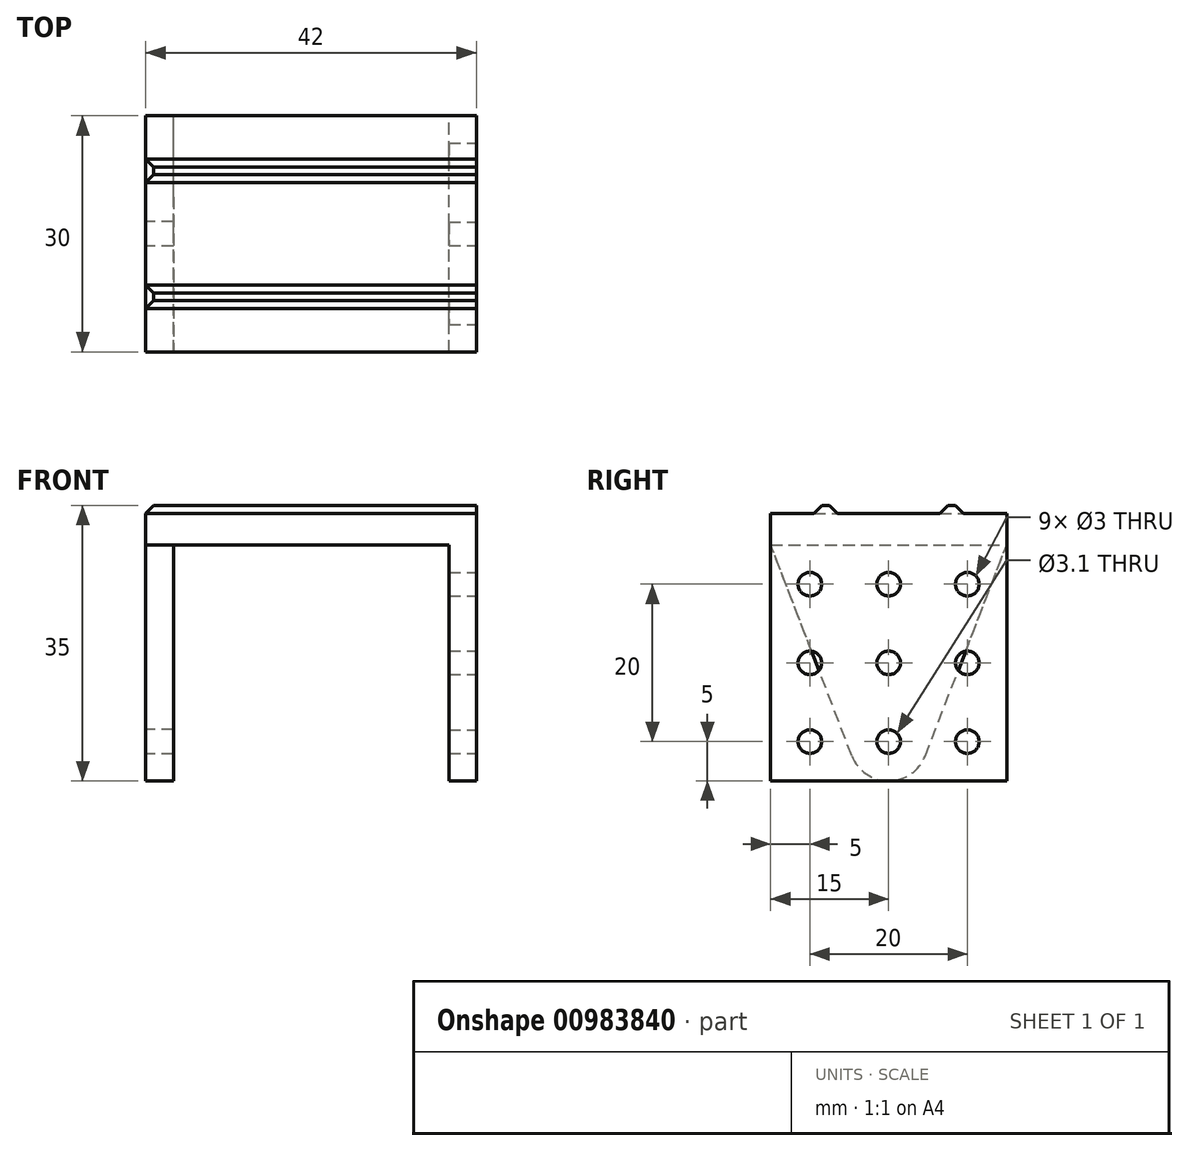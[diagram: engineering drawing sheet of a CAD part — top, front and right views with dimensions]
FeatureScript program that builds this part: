
annotation { "Feature Type Name" : "Feature", "Feature Type Description" : "" }
export const myFeature = defineFeature(function(context is Context, id is Id, definition is map)
    precondition{}
    {
        {
            var Q0;
            Q0=qCreatedBy(makeId("Top.planeOp"),FACE);
            var sketch = newSketch(context, id + "F0", { "sketchPlane" : qUnion([Q0])});
            skLineSegment(sketch, "E0.bottom", {"start": v(21, -15) * mm, "end": v(-21, -15) * mm});
            skLineSegment(sketch, "E0.top", {"start": v(21, 15) * mm, "end": v(-21, 15) * mm});
            skLineSegment(sketch, "E0.left", {"start": v(21, -15) * mm, "end": v(21, 15) * mm});
            skLineSegment(sketch, "E0.right", {"start": v(-21, -15) * mm, "end": v(-21, 15) * mm});
            skPoint(sketch, "E0.middle", {"position": v(0, 0) * mm});
            skSolve(sketch);
        }
        {
            var Q0;
            Q0 = qSketchRegion(id + "F0", true);
            extrude(context, id + "F1", {"entities" : qUnion([Q0]), "depth" : 4 * mm, "offsetDistance" : 25 * mm});
        }
        {
            var Q0;
            Q0=makeQuery(id+"F1.opExtrude","CAP_FACE",FACE,{"disambiguationData":[OSD([sQuery(id+"F0.wireOp",EDGE,"E0.bottom"),sQuery(id+"F0.wireOp",EDGE,"E0.top"),sQuery(id+"F0.wireOp",EDGE,"E0.left"),sQuery(id+"F0.wireOp",EDGE,"E0.right")])],"isStart":true});
            var sketch = newSketch(context, id + "F2", { "sketchPlane" : qUnion([Q0])});
            skLineSegment(sketch, "E1.bottom", {"start": v(-21, 15) * mm, "end": v(-17.5, 15) * mm});
            skLineSegment(sketch, "E1.top", {"start": v(-21, -15) * mm, "end": v(-17.5, -15) * mm});
            skLineSegment(sketch, "E1.left", {"start": v(-21, 15) * mm, "end": v(-21, -15) * mm});
            skLineSegment(sketch, "E1.right", {"start": v(-17.5, 15) * mm, "end": v(-17.5, -15) * mm});
            skLineSegment(sketch, "E2.bottom", {"start": v(21, 15) * mm, "end": v(17.5, 15) * mm});
            skLineSegment(sketch, "E2.top", {"start": v(21, -15) * mm, "end": v(17.5, -15) * mm});
            skLineSegment(sketch, "E2.left", {"start": v(21, 15) * mm, "end": v(21, -15) * mm});
            skLineSegment(sketch, "E2.right", {"start": v(17.5, 15) * mm, "end": v(17.5, -15) * mm});
            skSolve(sketch);
        }
        {
            var Q0;
            Q0=makeQuery(id+"F2.imprint","IMPRINT",FACE,{"disambiguationData":[TD([[makeQuery(id+"F2.imprint","IMPRINT",EDGE,{"derivedFrom":sQuery(id+"F2.wireOp",EDGE,"E1.bottom")}),1.0]])]});
            var Q1;
            Q1=makeQuery(id+"F2.imprint","IMPRINT",FACE,{"disambiguationData":[TD([[makeQuery(id+"F2.imprint","IMPRINT",EDGE,{"derivedFrom":sQuery(id+"F2.wireOp",EDGE,"E2.bottom")}),1.0]])]});
            extrude(context, id + "F3", {"entities" : qUnion([Q0, Q1]), "operationType" : NewBodyOperationType.ADD, "depth" : 30 * mm, "offsetDistance" : 25 * mm});
        }
        {
            var Q0;
            Q0=makeQuery(id+"F3.boolean.opBoolean","MERGE",FACE,{"derivedFrom":[makeQuery(id+"F1.opExtrude","SWEPT_FACE",FACE,{"disambiguationData":[OSD([sQuery(id+"F0.wireOp",EDGE,"E0.right")])]}),makeQuery(id+"F3.opExtrude","SWEPT_FACE",FACE,{"disambiguationData":[OSD([sQuery(id+"F2.wireOp",EDGE,"E1.left")])]})]});
            var sketch = newSketch(context, id + "F4", { "sketchPlane" : qUnion([Q0])});
            skCircle(sketch, "E3", {"center": v(0, -25) * mm, "radius": 1.55 * mm});
            skSolve(sketch);
        }
        {
            var Q0;
            Q0=makeQuery(id+"F4.imprint","IMPRINT",FACE,{"disambiguationData":[TD([[makeQuery(id+"F4.imprint","IMPRINT",EDGE,{"derivedFrom":sQuery(id+"F4.wireOp",EDGE,"E3")}),1.0]])]});
            extrude(context, id + "F5", {"entities" : qUnion([Q0]), "operationType" : NewBodyOperationType.REMOVE, "oppositeDirection" : true, "depth" : 5 * mm, "offsetDistance" : 25 * mm});
        }
        {
            var Q0;
            Q0=makeQuery(id+"F3.boolean.opBoolean","MERGE",FACE,{"derivedFrom":[makeQuery(id+"F1.opExtrude","SWEPT_FACE",FACE,{"disambiguationData":[OSD([sQuery(id+"F0.wireOp",EDGE,"E0.right")])]}),makeQuery(id+"F3.opExtrude","SWEPT_FACE",FACE,{"disambiguationData":[OSD([sQuery(id+"F2.wireOp",EDGE,"E1.left")])]})]});
            var sketch = newSketch(context, id + "F6", { "sketchPlane" : qUnion([Q0])});
            skArc(sketch, "E4", {"start": v(-4.67, -26.8) * mm, "mid": v(0, -30) * mm, "end": v(4.67, -26.8) * mm});
            skLineSegment(sketch, "E5", {"start": v(-4.67, -26.8) * mm, "end": v(-15, 0) * mm});
            skLineSegment(sketch, "E6", {"start": v(4.67, -26.8) * mm, "end": v(15, 0) * mm});
            skSolve(sketch);
        }
        {
            var Q0;
            {var subQ0=sQuery(id+"F6.wireOp",EDGE,"E5");Q0=makeQuery(id+"F6.imprint","IMPRINT",FACE,{"disambiguationData":[TD([[makeQuery(id+"F6.imprint","IMPRINT",EDGE,{"derivedFrom":subQ0}),1.0]])]});}
            var Q1;
            {var subQ0=sQuery(id+"F6.wireOp",EDGE,"E6");Q1=makeQuery(id+"F6.imprint","IMPRINT",FACE,{"disambiguationData":[TD([[makeQuery(id+"F6.imprint","IMPRINT",EDGE,{"derivedFrom":subQ0}),-1.0]])]});}
            extrude(context, id + "F7", {"entities" : qUnion([Q0, Q1]), "operationType" : NewBodyOperationType.REMOVE, "oppositeDirection" : true, "depth" : 3.5 * mm, "offsetDistance" : 25 * mm});
        }
        {
            var Q0;
            Q0=makeQuery(id+"F1.opExtrude","CAP_FACE",FACE,{"disambiguationData":[OSD([sQuery(id+"F0.wireOp",EDGE,"E0.bottom"),sQuery(id+"F0.wireOp",EDGE,"E0.top"),sQuery(id+"F0.wireOp",EDGE,"E0.left"),sQuery(id+"F0.wireOp",EDGE,"E0.right")])],"isStart":false});
            var sketch = newSketch(context, id + "F8", { "sketchPlane" : qUnion([Q0])});
            skLineSegment(sketch, "E7.bottom", {"start": v(-21, 10) * mm, "end": v(21, 10) * mm});
            skLineSegment(sketch, "E7.top", {"start": v(-21, 6) * mm, "end": v(21, 6) * mm});
            skLineSegment(sketch, "E7.left", {"start": v(-21, 10) * mm, "end": v(-21, 6) * mm});
            skLineSegment(sketch, "E7.right", {"start": v(21, 10) * mm, "end": v(21, 6) * mm});
            skLineSegment(sketch, "E8.bottom", {"start": v(-21, -6) * mm, "end": v(21, -6) * mm});
            skLineSegment(sketch, "E8.top", {"start": v(-21, -10) * mm, "end": v(21, -10) * mm});
            skLineSegment(sketch, "E8.left", {"start": v(-21, -6) * mm, "end": v(-21, -10) * mm});
            skLineSegment(sketch, "E8.right", {"start": v(21, -6) * mm, "end": v(21, -10) * mm});
            skSolve(sketch);
        }
        {
            var Q0;
            Q0 = qSketchRegion(id + "F8", true);
            extrude(context, id + "F9", {"entities" : qUnion([Q0]), "operationType" : NewBodyOperationType.ADD, "depth" : 1 * mm, "offsetDistance" : 25 * mm});
        }
        {
            var Q0;
            Q0=makeQuery(id+"F9.opExtrude","CAP_EDGE",EDGE,{"disambiguationData":[OSD([sQuery(id+"F8.wireOp",EDGE,"E8.left")])],"isStart":false});
            var Q1;
            Q1=makeQuery(id+"F9.opExtrude","CAP_EDGE",EDGE,{"disambiguationData":[OSD([sQuery(id+"F8.wireOp",EDGE,"E7.left")])],"isStart":false});
            chamfer(context, id + "F10", {"entities" : qUnion([Q0, Q1]), "width" : 1 * mm, "tangentPropagation" : true});
        }
        {
            var Q0;
            Q0=makeQuery(id+"F9.opExtrude","CAP_EDGE",EDGE,{"disambiguationData":[OSD([sQuery(id+"F8.wireOp",EDGE,"E8.top")])],"isStart":false});
            var Q1;
            Q1=makeQuery(id+"F9.opExtrude","CAP_EDGE",EDGE,{"disambiguationData":[OSD([sQuery(id+"F8.wireOp",EDGE,"E8.bottom")])],"isStart":false});
            var Q2;
            Q2=makeQuery(id+"F9.opExtrude","CAP_EDGE",EDGE,{"disambiguationData":[OSD([sQuery(id+"F8.wireOp",EDGE,"E7.top")])],"isStart":false});
            var Q3;
            Q3=makeQuery(id+"F9.opExtrude","CAP_EDGE",EDGE,{"disambiguationData":[OSD([sQuery(id+"F8.wireOp",EDGE,"E7.bottom")])],"isStart":false});
            chamfer(context, id + "F11", {"entities" : qUnion([Q0, Q1, Q2, Q3]), "width" : 1.5 * mm, "tangentPropagation" : true});
        }
        {
            var Q0;
            Q0=makeQuery(id+"F9.boolean.opBoolean","MERGE",FACE,{"derivedFrom":[makeQuery(id+"F3.boolean.opBoolean","MERGE",FACE,{"derivedFrom":[makeQuery(id+"F1.opExtrude","SWEPT_FACE",FACE,{"disambiguationData":[OSD([sQuery(id+"F0.wireOp",EDGE,"E0.left")])]}),makeQuery(id+"F3.opExtrude","SWEPT_FACE",FACE,{"disambiguationData":[OSD([sQuery(id+"F2.wireOp",EDGE,"E2.left")])]})]}),makeQuery(id+"F9.opExtrude","SWEPT_FACE",FACE,{"disambiguationData":[OSD([sQuery(id+"F8.wireOp",EDGE,"E7.right")])]}),makeQuery(id+"F9.opExtrude","SWEPT_FACE",FACE,{"disambiguationData":[OSD([sQuery(id+"F8.wireOp",EDGE,"E8.right")])]})]});
            var sketch = newSketch(context, id + "F12", { "sketchPlane" : qUnion([Q0])});
            skCircle(sketch, "E9", {"center": v(-10, -5) * mm, "radius": 1.5 * mm});
            skCircle(sketch, "E10.1.0.0", {"center": v(0, -5) * mm, "radius": 1.5 * mm});
            skCircle(sketch, "E10.2.0.0", {"center": v(10, -5) * mm, "radius": 1.5 * mm});
            skLineSegment(sketch, "E10.direction1", {"start": v(-10, -5) * mm, "end": v(0, -5) * mm, "construction": true});
            skLineSegment(sketch, "E11", {"start": v(-10, -5) * mm, "end": v(-10, -24.82) * mm});
            skCircle(sketch, "E12.1.0.0", {"center": v(-10, -15) * mm, "radius": 1.5 * mm});
            skCircle(sketch, "E12.2.0.0", {"center": v(-10, -25) * mm, "radius": 1.5 * mm});
            skLineSegment(sketch, "E12.direction1", {"start": v(-10, -5) * mm, "end": v(-10, -15) * mm, "construction": true});
            skCircle(sketch, "E13.1.0.0", {"center": v(0, -15) * mm, "radius": 1.5 * mm});
            skCircle(sketch, "E13.1.0.1", {"center": v(0, -25) * mm, "radius": 1.5 * mm});
            skCircle(sketch, "E13.2.0.0", {"center": v(10, -15) * mm, "radius": 1.5 * mm});
            skCircle(sketch, "E13.2.0.1", {"center": v(10, -25) * mm, "radius": 1.5 * mm});
            skLineSegment(sketch, "E13.direction1", {"start": v(-10, -15) * mm, "end": v(0, -15) * mm, "construction": true});
            skSolve(sketch);
        }
        {
            var Q0;
            Q0 = qSketchRegion(id + "F12", true);
            extrude(context, id + "F13", {"entities" : qUnion([Q0]), "operationType" : NewBodyOperationType.REMOVE, "oppositeDirection" : true, "depth" : 3.5 * mm, "offsetDistance" : 25 * mm});
        }
    });
